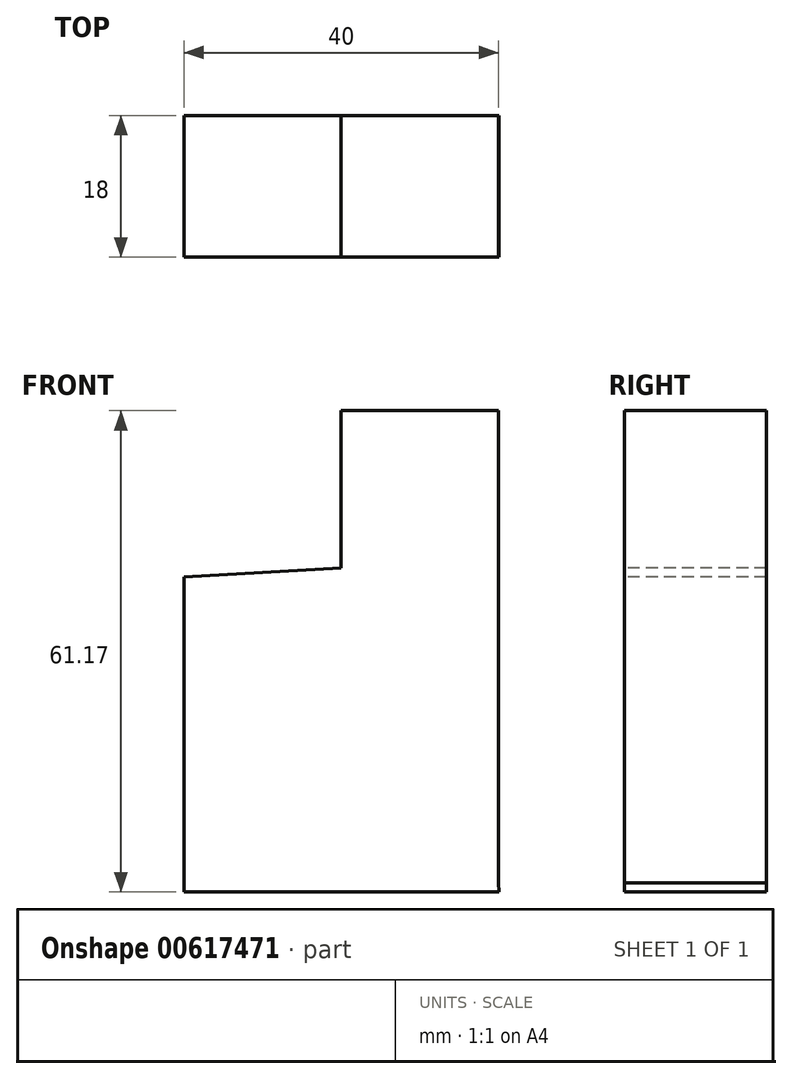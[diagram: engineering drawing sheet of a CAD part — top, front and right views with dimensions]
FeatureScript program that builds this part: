
annotation { "Feature Type Name" : "Feature", "Feature Type Description" : "" }
export const myFeature = defineFeature(function(context is Context, id is Id, definition is map)
    precondition{}
    {
        {
            var Q0;
            Q0=qCreatedBy(makeId("Front.planeOp"),FACE);
            var sketch = newSketch(context, id + "F0", { "sketchPlane" : qUnion([Q0])});
            skLineSegment(sketch, "E0", {"start": v(-32.5, 14.5) * mm, "end": v(-32.5, -25.5) * mm});
            skLineSegment(sketch, "E1", {"start": v(-32.5, -25.5) * mm, "end": v(7.5, -25.5) * mm});
            skLineSegment(sketch, "E2", {"start": v(7.47, -24.34) * mm, "end": v(7.47, 35.66) * mm});
            skLineSegment(sketch, "E3", {"start": v(7.47, 35.66) * mm, "end": v(-12.53, 35.66) * mm});
            skLineSegment(sketch, "E4", {"start": v(-12.53, 35.66) * mm, "end": v(-12.53, 15.66) * mm});
            skLineSegment(sketch, "E5", {"start": v(-32.5, 14.5) * mm, "end": v(-12.53, 15.66) * mm});
            skLineSegment(sketch, "E6", {"start": v(7.47, -24.34) * mm, "end": v(7.5, -25.5) * mm});
            skSolve(sketch);
        }
        {
            var Q0;
            {var subQ4=sQuery(id+"F0.wireOp",EDGE,"E0");Q0=makeQuery(id+"F0.imprint","IMPRINT",FACE,{"disambiguationData":[TD([[makeQuery(id+"F0.imprint","IMPRINT",EDGE,{"derivedFrom":subQ4}),1.0]])]});}
            extrude(context, id + "F1", {"entities" : qUnion([Q0]), "oppositeDirection" : true, "depth" : 18 * mm, "offsetDistance" : 25 * mm});
        }
    });
